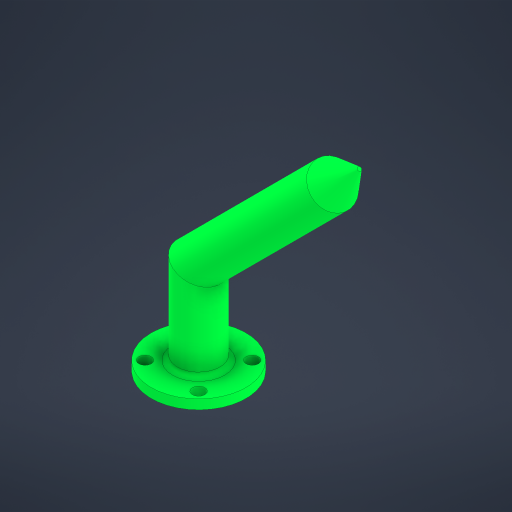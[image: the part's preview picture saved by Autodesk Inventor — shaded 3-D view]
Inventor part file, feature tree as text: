
AUTODESK INVENTOR PART (.ipt)
format: ipt  version: 2023.4 (Build 274418000, 418)  size: 233,984 bytes
history: native  units: mm
features: sketch x5, sweep x1, extrude x1, hole x1, fillet x1, plane x1, loft x1, other x1
ambient origin geometry x8: Origin, YZ Plane, XZ Plane, XY Plane, X Axis, Y Axis, Z Axis, Center Point
bodies: Solid1 (feature_tree)
feature tree (12):
  sweep  "Sweep1"
  sketch  "Sketch3"  dims[d6=17.5mm d7=2.5mm d8=40.0mm]
  extrude  "Extrusion1"  TaperAngle=0.0deg  [1 undecoded]
  hole  "Hole1"  [1 undecoded]
  fillet  "Fillet1"  Radius=40.0mm
  plane  "Work Plane1"
  loft  "Loft2"
  sketch  "Sketch1"  dims[d0=50.0mm d1=100.0mm]
  sketch  "Sketch2"  dims[d2=45.0deg d4=0.0mm d5=0.0mm]
  sketch  "Sketch4"  dims[d9=5.0mm d10=50.0mm]
  sketch  "Sketch8"  dims[d11=5.0mm d12=0.0mm d13=6.6mm d14=12.0mm d15=14.55mm d16=4.15mm d17=90.0deg d18=8.0mm d19=20.594885mm d24=120.0mm d26=2.5mm d27=22.5mm d34=2.0mm d35=0.0mm d36=90.0deg d37=0.0mm d38=90.0deg]
  other  "Edges2"
note: 2 required parameter values undecoded (feature->parameter linkage not recoverable at this tier; creation-order binding heuristic only, values carry confidence <= 0.55)
